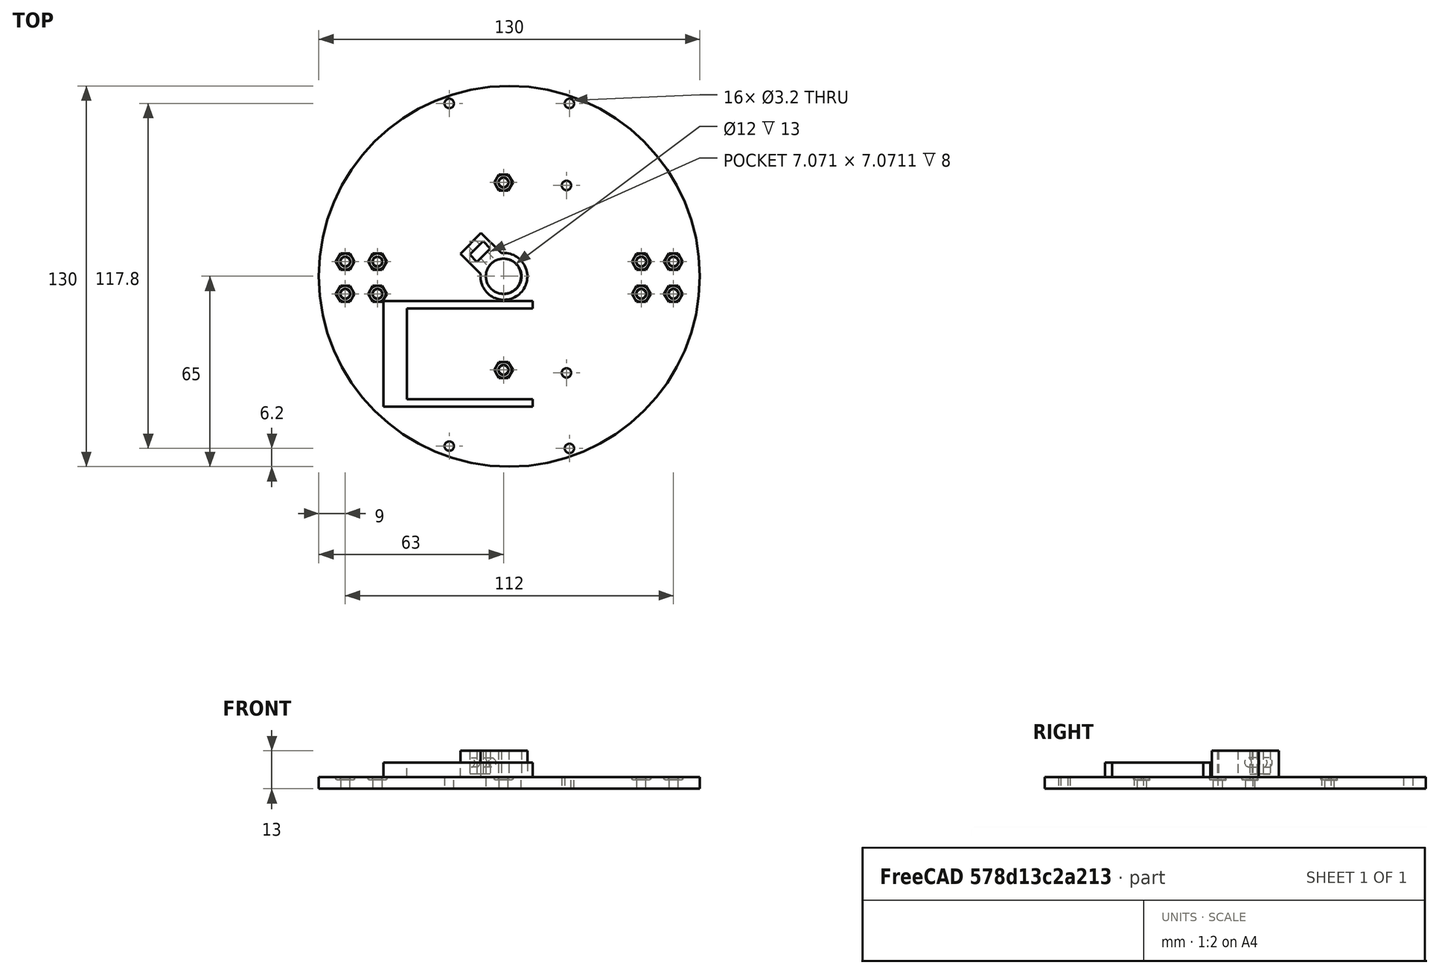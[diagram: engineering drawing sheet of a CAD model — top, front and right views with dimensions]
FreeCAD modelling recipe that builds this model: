
FCSTD DOCUMENT  (FreeCAD 0.21R33668 +26 (Git))
Label: plataformaInferiorPenHolder
License: All rights reserved
LicenseURL: https://en.wikipedia.org/wiki/All_rights_reserved
objects: Part::Cylinder×21, Part::MultiFuse×15, Part::FeaturePython×10, Part::Cut×6, Part::Box×4, Part::Feature×1, Mesh::Feature×1
note: 57 computed .brp shape members not serialized (recipe doc carries the construction recipe); baked Part::Feature solids carry a one-line shape summary decoded from their .brp

FEATURE [Part::Cylinder] Cylinder004  label="Cilindro004"
  Angle = 360
  AttacherType = Attacher::AttachEngine3D
  FirstAngle = 0
  Height = 4
  Placement = pos=(-4,0,-15) rot=(0,0,1;0rad)
  Radius = 65
  SecondAngle = 0
FEATURE [Part::Cylinder] Cylinder082  label="Cilindro082"
  Angle = 360
  AttacherType = Attacher::AttachEngine3D
  FirstAngle = 0
  Height = 10
  Placement = pos=(32,-6,-20) rot=(0,0,1;0rad)
  Radius = 1.6
  SecondAngle = 0
FEATURE [Part::Cylinder] Cylinder083  label="Cilindro083"
  Angle = 360
  AttacherType = Attacher::AttachEngine3D
  FirstAngle = 0
  Height = 10
  Placement = pos=(32,5,-20) rot=(0,0,1;0rad)
  Radius = 1.6
  SecondAngle = 0
FEATURE [Part::Cylinder] Cylinder084  label="Cilindro084"
  Angle = 360
  AttacherType = Attacher::AttachEngine3D
  FirstAngle = 0
  Height = 10
  Placement = pos=(21,-6,-20) rot=(0,0,1;0rad)
  Radius = 1.6
  SecondAngle = 0
FEATURE [Part::Cylinder] Cylinder085  label="Cilindro085"
  Angle = 360
  AttacherType = Attacher::AttachEngine3D
  FirstAngle = 0
  Height = 10
  Placement = pos=(21,5,-20) rot=(0,0,1;0rad)
  Radius = 1.6
  SecondAngle = 0
FEATURE [Part::Cylinder] Cylinder086  label="Cilindro086"
  Angle = 360
  AttacherType = Attacher::AttachEngine3D
  FirstAngle = 0
  Height = 10
  Placement = pos=(32,-6,-20) rot=(0,0,1;0rad)
  Radius = 1.6
  SecondAngle = 0
FEATURE [Part::Cylinder] Cylinder087  label="Cilindro087"
  Angle = 360
  AttacherType = Attacher::AttachEngine3D
  FirstAngle = 0
  Height = 10
  Placement = pos=(32,5,-20) rot=(0,0,1;0rad)
  Radius = 1.6
  SecondAngle = 0
FEATURE [Part::Cylinder] Cylinder088  label="Cilindro088"
  Angle = 360
  AttacherType = Attacher::AttachEngine3D
  FirstAngle = 0
  Height = 10
  Placement = pos=(21,-6,-20) rot=(0,0,1;0rad)
  Radius = 1.6
  SecondAngle = 0
FEATURE [Part::Cylinder] Cylinder089  label="Cilindro089"
  Angle = 360
  AttacherType = Attacher::AttachEngine3D
  FirstAngle = 0
  Height = 10
  Placement = pos=(21,5,-20) rot=(0,0,1;0rad)
  Radius = 1.6
  SecondAngle = 0
FEATURE [Part::Cylinder] Cylinder090  label="Cilindro090"
  Angle = 360
  AttacherType = Attacher::AttachEngine3D
  FirstAngle = 0
  Height = 10
  Placement = pos=(-6,-32,-19) rot=(0,0,1;0rad)
  Radius = 1.6
  SecondAngle = 0
FEATURE [Part::Cylinder] Cylinder091  label="Cilindro091"
  Angle = 360
  AttacherType = Attacher::AttachEngine3D
  FirstAngle = 0
  Height = 10
  Placement = pos=(-6,32,-19) rot=(0,0,1;0rad)
  Radius = 1.6
  SecondAngle = 0
FEATURE [Part::Cylinder] Cylinder092  label="Cilindro092"
  Angle = 360
  AttacherType = Attacher::AttachEngine3D
  FirstAngle = 0
  Height = 50
  Placement = pos=(16.5,-58.8,-17) rot=(0,0,1;0rad)
  Radius = 1.6
  SecondAngle = 0
FEATURE [Part::Cylinder] Cylinder093  label="Cilindro093"
  Angle = 360
  AttacherType = Attacher::AttachEngine3D
  FirstAngle = 0
  Height = 50
  Placement = pos=(16.5,59,-17) rot=(0,0,1;0rad)
  Radius = 1.6
  SecondAngle = 0
FEATURE [Part::Cylinder] Cylinder094  label="Cilindro094"
  Angle = 360
  AttacherType = Attacher::AttachEngine3D
  FirstAngle = 0
  Height = 50
  Placement = pos=(-24.5,59,-17) rot=(0,0,1;0rad)
  Radius = 1.6
  SecondAngle = 0
FEATURE [Part::Cylinder] Cylinder095  label="Cilindro095"
  Angle = 360
  AttacherType = Attacher::AttachEngine3D
  FirstAngle = 0
  Height = 50
  Placement = pos=(-24.5,-58,-17) rot=(0,0,1;0rad)
  Radius = 1.6
  SecondAngle = 0
FEATURE [Part::Cylinder] Cylinder096  label="Cilindro096"
  Angle = 360
  AttacherType = Attacher::AttachEngine3D
  FirstAngle = 0
  Height = 50
  Placement = pos=(15.5,-33,-17) rot=(0,0,1;0rad)
  Radius = 1.6
  SecondAngle = 0
FEATURE [Part::Cylinder] Cylinder097  label="Cilindro097"
  Angle = 360
  AttacherType = Attacher::AttachEngine3D
  FirstAngle = 0
  Height = 50
  Placement = pos=(15.5,31,-17) rot=(0,0,1;0rad)
  Radius = 1.6
  SecondAngle = 0
FEATURE [Part::Cylinder] Cylinder098  label="Cilindro098"
  Angle = 360
  AttacherType = Attacher::AttachEngine3D
  FirstAngle = 0
  Height = 20
  Placement = pos=(-6,0,-20) rot=(0,0,1;0rad)
  Radius = 6
  SecondAngle = 0
FEATURE [Part::MultiFuse] Fusion044
  Placement = pos=(20,0,0) rot=(0,0,1;0rad)
  Shapes = -> [Cylinder082,Cylinder083,Cylinder084,Cylinder085]
FEATURE [Part::MultiFuse] Fusion045
  Placement = pos=(-81,0,0) rot=(0,0,1;0rad)
  Shapes = -> [Cylinder086,Cylinder087,Cylinder088,Cylinder089]
FEATURE [Part::MultiFuse] Fusion046
  Shapes = -> [Fusion044,Fusion045]
FEATURE [Part::MultiFuse] Fusion048  label="taladrosAbajo001"
  Shapes = -> [Cylinder092,Cylinder093,Cylinder094,Cylinder095]
FEATURE [Part::MultiFuse] Fusion050
  Shapes = -> [Cylinder097,Cylinder096]
FEATURE [Part::FeaturePython] Nut017  label="M3-Tuerca017"  # Fasteners workbench fastener (typed FeaturePython)
  Placement = pos=(-6,-32,-12) rot=(0,0,1;0rad)
  diameter = 4
  invert = false
  leftHanded = false
  matchOuter = false
  offset = 0
  thread = false
  type = 22
FEATURE [Part::FeaturePython] Nut018  label="M3-Tuerca018"  # Fasteners workbench fastener (typed FeaturePython)
  Placement = pos=(32,5,-12) rot=(0,0,1;0rad)
  diameter = 4
  invert = false
  leftHanded = false
  matchOuter = false
  offset = 0
  thread = false
  type = 24
FEATURE [Part::FeaturePython] Nut019  label="M3-Tuerca019"  # Fasteners workbench fastener (typed FeaturePython)
  Placement = pos=(21,5,-12) rot=(0,0,1;0rad)
  diameter = 4
  invert = false
  leftHanded = false
  matchOuter = false
  offset = 0
  thread = false
  type = 24
FEATURE [Part::FeaturePython] Nut020  label="M3-Tuerca020"  # Fasteners workbench fastener (typed FeaturePython)
  Placement = pos=(32,-6,-12) rot=(0,0,1;0rad)
  diameter = 4
  invert = false
  leftHanded = false
  matchOuter = false
  offset = 0
  thread = false
  type = 24
FEATURE [Part::FeaturePython] Nut021  label="M3-Tuerca021"  # Fasteners workbench fastener (typed FeaturePython)
  Placement = pos=(21,-6,-12) rot=(0,0,1;0rad)
  diameter = 4
  invert = false
  leftHanded = false
  matchOuter = false
  offset = 0
  thread = false
  type = 24
FEATURE [Part::MultiFuse] Fusion041
  Placement = pos=(20,0,0) rot=(0,0,1;0rad)
  Shapes = -> [Nut021,Nut020,Nut019,Nut018]
FEATURE [Part::FeaturePython] Nut022  label="M3-Tuerca022"  # Fasteners workbench fastener (typed FeaturePython)
  Placement = pos=(32,5,-12) rot=(0,0,1;0rad)
  diameter = 4
  invert = false
  leftHanded = false
  matchOuter = false
  offset = 0
  thread = false
  type = 24
FEATURE [Part::FeaturePython] Nut023  label="M3-Tuerca023"  # Fasteners workbench fastener (typed FeaturePython)
  Placement = pos=(21,5,-12) rot=(0,0,1;0rad)
  diameter = 4
  invert = false
  leftHanded = false
  matchOuter = false
  offset = 0
  thread = false
  type = 24
FEATURE [Part::FeaturePython] Nut024  label="M3-Tuerca024"  # Fasteners workbench fastener (typed FeaturePython)
  Placement = pos=(32,-6,-12) rot=(0,0,1;0rad)
  diameter = 4
  invert = false
  leftHanded = false
  matchOuter = false
  offset = 0
  thread = false
  type = 24
FEATURE [Part::FeaturePython] Nut025  label="M3-Tuerca025"  # Fasteners workbench fastener (typed FeaturePython)
  Placement = pos=(21,-6,-12) rot=(0,0,1;0rad)
  diameter = 4
  invert = false
  leftHanded = false
  matchOuter = false
  offset = 0
  thread = false
  type = 24
FEATURE [Part::MultiFuse] Fusion042
  Placement = pos=(-81,0,0) rot=(0,0,1;0rad)
  Shapes = -> [Nut025,Nut024,Nut023,Nut022]
FEATURE [Part::MultiFuse] Fusion043
  Shapes = -> [Fusion042,Fusion041]
FEATURE [Part::FeaturePython] Nut026  label="M3-Tuerca026"  # Fasteners workbench fastener (typed FeaturePython)
  Placement = pos=(-6,32,-12) rot=(0,0,1;0rad)
  diameter = 4
  invert = false
  leftHanded = false
  matchOuter = false
  offset = 0
  thread = false
  type = 22
FEATURE [Part::MultiFuse] Fusion040
  Shapes = -> [Nut026,Nut017,Cylinder091,Cylinder090]
FEATURE [Part::MultiFuse] Fusion047
  Shapes = -> [Fusion040,Fusion046,Fusion043]
FEATURE [Part::MultiFuse] Fusion049
  Shapes = -> [Fusion047,Fusion048]
FEATURE [Part::Cut] Cut  label="plataformaInterior"
  Base = -> Cylinder004
  Tool = -> Fusion049
FEATURE [Part::Cut] Cut003  label="plataformaInf"
  Base = -> Cut
  Tool = -> Fusion050
FEATURE [Part::Box] Box  label="Cubo"
  AttacherType = Attacher::AttachEngine3D
  Height = 10
  Length = 10
  Placement = pos=(0,-5,-12) rot=(0,0,1;0rad)
  Width = 10
FEATURE [Part::Box] Box015  label="Cubo015"
  AttacherType = Attacher::AttachEngine3D
  Height = 3.5
  Length = 10
  Placement = pos=(4,-3.5,0) rot=(0,1,0;1.5708rad)
  Width = 6.5
FEATURE [Part::Cylinder] Cylinder059  label="Cilindro059"
  Angle = 360
  AttacherType = Attacher::AttachEngine3D
  FirstAngle = 0
  Height = 20
  Placement = pos=(-1.5,-0.3,-6) rot=(0,1,0;1.5708rad)
  Radius = 1.6
  SecondAngle = 0
FEATURE [Part::Cylinder] Cylinder081  label="Cilindro081"
  Angle = 360
  AttacherType = Attacher::AttachEngine3D
  FirstAngle = 0
  Height = 10
  Placement = pos=(-6,0,-12) rot=(0,0,1;0rad)
  Radius = 8
  SecondAngle = 0
FEATURE [Part::Cylinder] Cylinder099  label="Cilindro099"
  Angle = 360
  AttacherType = Attacher::AttachEngine3D
  FirstAngle = 0
  Height = 20
  Placement = pos=(-6,0,-20) rot=(0,0,1;0rad)
  Radius = 6
  SecondAngle = 0
FEATURE [Part::Cut] Cut004
  Base = -> Cylinder081
  Tool = -> Cylinder099
FEATURE [Part::MultiFuse] Fusion
  Shapes = -> [Cut004,Box]
FEATURE [Part::MultiFuse] Fusion058
  Shapes = -> [Cylinder059,Box015]
FEATURE [Part::Cut] Cut019  label="penHolder"
  Base = -> Fusion
  Placement = pos=(-10.1,4.2,0) rot=(0,0,1;2.35619rad)
  Tool = -> Fusion058
FEATURE [Part::MultiFuse] Fusion059
  Shapes = -> [Cut003,Cut019]
FEATURE [Part::Cut] Cut020  label="platInf2"
  Base = -> Fusion059
  Tool = -> Cylinder098
FEATURE [Part::Box] Box028  label="portapilasx6"
  AttacherType = Attacher::AttachEngine3D
  Height = 60
  Length = 45
  Placement = pos=(-37,-44,-10) rot=(0,0,1;0rad)
  Width = 31
FEATURE [Part::Box] Box029  label="Cubo016"
  AttacherType = Attacher::AttachEngine3D
  Height = 6
  Length = 51
  Placement = pos=(-45,-46.5,0) rot=(0,0,1;0rad)
  Width = 36
FEATURE [Part::Cut] Cut021
  Base = -> Box029
  Placement = pos=(-2,2,-12) rot=(0,0,1;0rad)
  Tool = -> Box028
FEATURE [Part::MultiFuse] Fusion060  label="plataformaInferior"
  Shapes = -> [Cut020,Cut021]
FEATURE [Part::Feature] Fusion060_solid  label="plataformaInferior (Solid)"
  shape: bbox 130 x 130 x 13 mm, 195 faces (baked)
FEATURE [Mesh::Feature] Mesh  label="plataformaInferior (Solid) (Meshed)"
